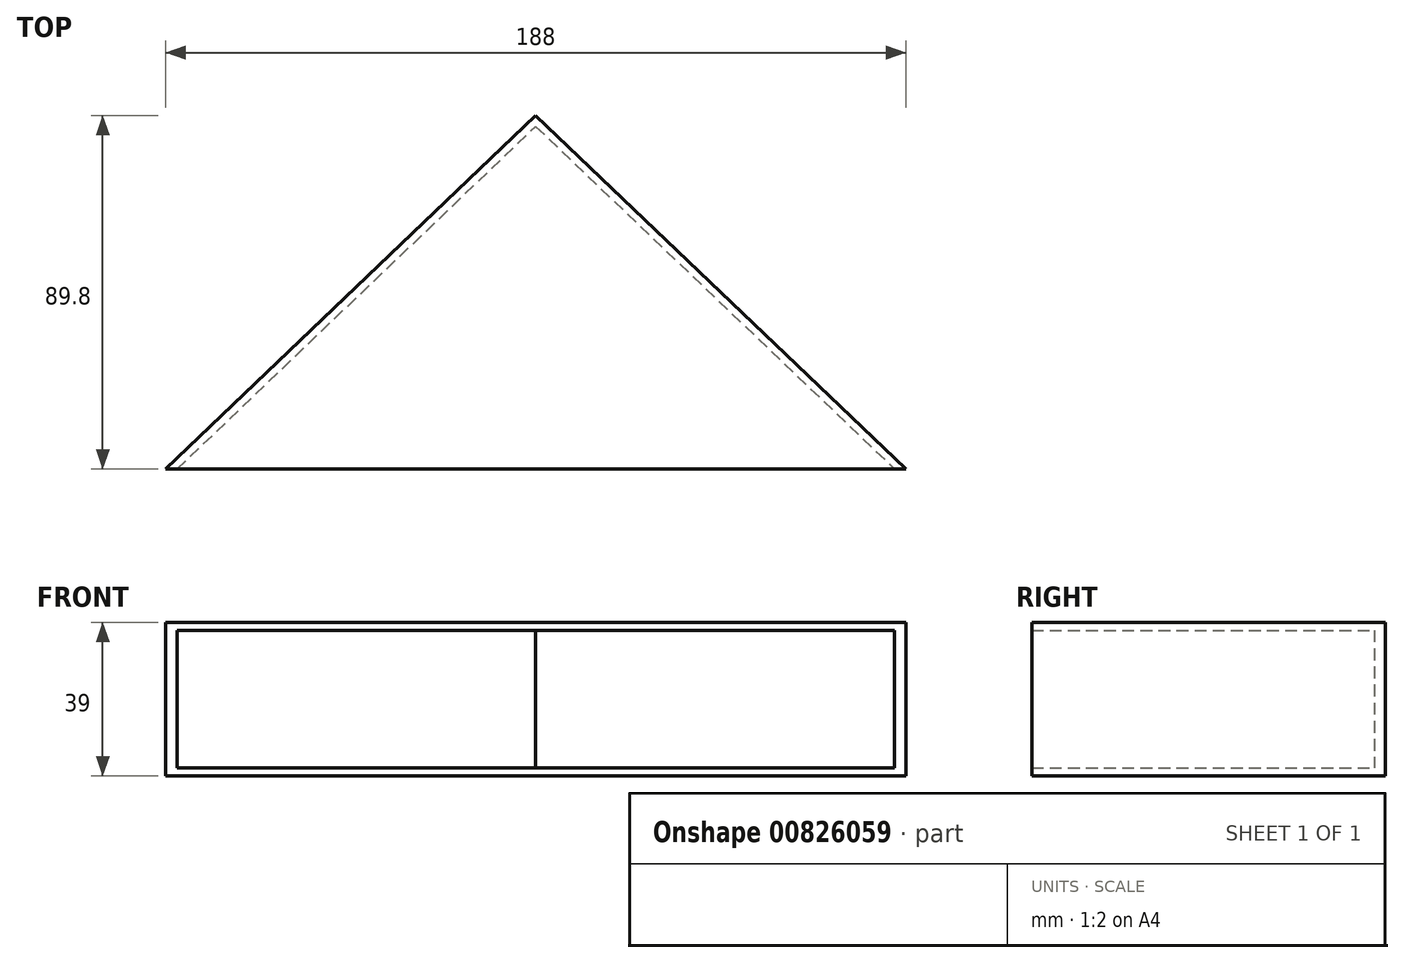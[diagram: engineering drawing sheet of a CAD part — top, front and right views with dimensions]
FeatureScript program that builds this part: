
annotation { "Feature Type Name" : "Feature", "Feature Type Description" : "" }
export const myFeature = defineFeature(function(context is Context, id is Id, definition is map)
    precondition{}
    {
        {
            var Q0;
            Q0=qCreatedBy(makeId("Top.planeOp"),FACE);
            var sketch = newSketch(context, id + "F0", { "sketchPlane" : qUnion([Q0])});
            skLineSegment(sketch, "E0", {"start": v(94, 0) * mm, "end": v(0, 89.8) * mm});
            skLineSegment(sketch, "E1", {"start": v(0, 89.8) * mm, "end": v(-94, 0) * mm});
            skLineSegment(sketch, "E2", {"start": v(-94, 0) * mm, "end": v(94, 0) * mm});
            skSolve(sketch);
        }
        {
            var Q0;
            Q0=makeQuery(id+"F0.imprint","IMPRINT",FACE,{"disambiguationData":[TD([[makeQuery(id+"F0.imprint","IMPRINT",EDGE,{"derivedFrom":sQuery(id+"F0.wireOp",EDGE,"E0")}),1.0]])]});
            extrude(context, id + "F1", {"entities" : qUnion([Q0]), "depth" : 2 * mm, "offsetDistance" : 25 * mm});
        }
        {
            var Q0;
            Q0=makeQuery(id+"F1.opExtrude","CAP_FACE",FACE,{"disambiguationData":[OSD([sQuery(id+"F0.wireOp",EDGE,"E0"),sQuery(id+"F0.wireOp",EDGE,"E1"),sQuery(id+"F0.wireOp",EDGE,"E2")])],"isStart":false});
            var sketch = newSketch(context, id + "F2", { "sketchPlane" : qUnion([Q0])});
            skLineSegment(sketch, "E3", {"start": v(0, 87.03) * mm, "end": v(91.1, 0) * mm});
            skLineSegment(sketch, "E4", {"start": v(-91.1, 0) * mm, "end": v(0, 87.03) * mm});
            skSolve(sketch);
        }
        {
            var Q0;
            Q0=makeQuery(id+"F2.imprint","IMPRINT",FACE,{"disambiguationData":[TD([[makeQuery(id+"F2.imprint","IMPRINT",EDGE,{"derivedFrom":sQuery(id+"F2.wireOp",EDGE,"E3")}),1.0]])]});
            extrude(context, id + "F3", {"entities" : qUnion([Q0]), "operationType" : NewBodyOperationType.ADD, "depth" : 35 * mm, "offsetDistance" : 25 * mm});
        }
        {
            var Q0;
            Q0=makeQuery(id+"F3.opExtrude","CAP_FACE",FACE,{"disambiguationData":[OSD([sQuery(id+"F0.wireOp",EDGE,"E0"),sQuery(id+"F0.wireOp",EDGE,"E1"),sQuery(id+"F0.wireOp",EDGE,"E2"),sQuery(id+"F2.wireOp",EDGE,"E3"),sQuery(id+"F2.wireOp",EDGE,"E4")])],"isStart":false});
            var sketch = newSketch(context, id + "F4", { "sketchPlane" : qUnion([Q0])});
            skLineSegment(sketch, "E5", {"start": v(94, 0) * mm, "end": v(-94, 0) * mm});
            skSolve(sketch);
        }
        {
            var Q0;
            Q0 = qSketchRegion(id + "F4", true);
            var Q1;
            {var subQ1=makeQuery(id+"F3.opExtrude","CAP_EDGE",EDGE,{"disambiguationData":[OSD([sQuery(id+"F2.wireOp",EDGE,"E3")])],"isStart":false});Q1=makeQuery(id+"F4.imprint","IMPRINT",FACE,{"disambiguationData":[TD([[makeQuery(id+"F4.imprint","IMPRINT",EDGE,{"derivedFrom":subQ1}),-1.0]])]});}
            var Q2;
            {var subQ1=makeQuery(id+"F3.opExtrude","CAP_EDGE",EDGE,{"disambiguationData":[OSD([sQuery(id+"F2.wireOp",EDGE,"E3")])],"isStart":false});Q2=makeQuery(id+"F4.imprint","IMPRINT",FACE,{"disambiguationData":[TD([[makeQuery(id+"F4.imprint","IMPRINT",EDGE,{"derivedFrom":subQ1}),1.0]])]});}
            extrude(context, id + "F5", {"entities" : qUnion([Q0, Q1, Q2]), "operationType" : NewBodyOperationType.ADD, "depth" : 2 * mm, "offsetDistance" : 25 * mm});
        }
    });
